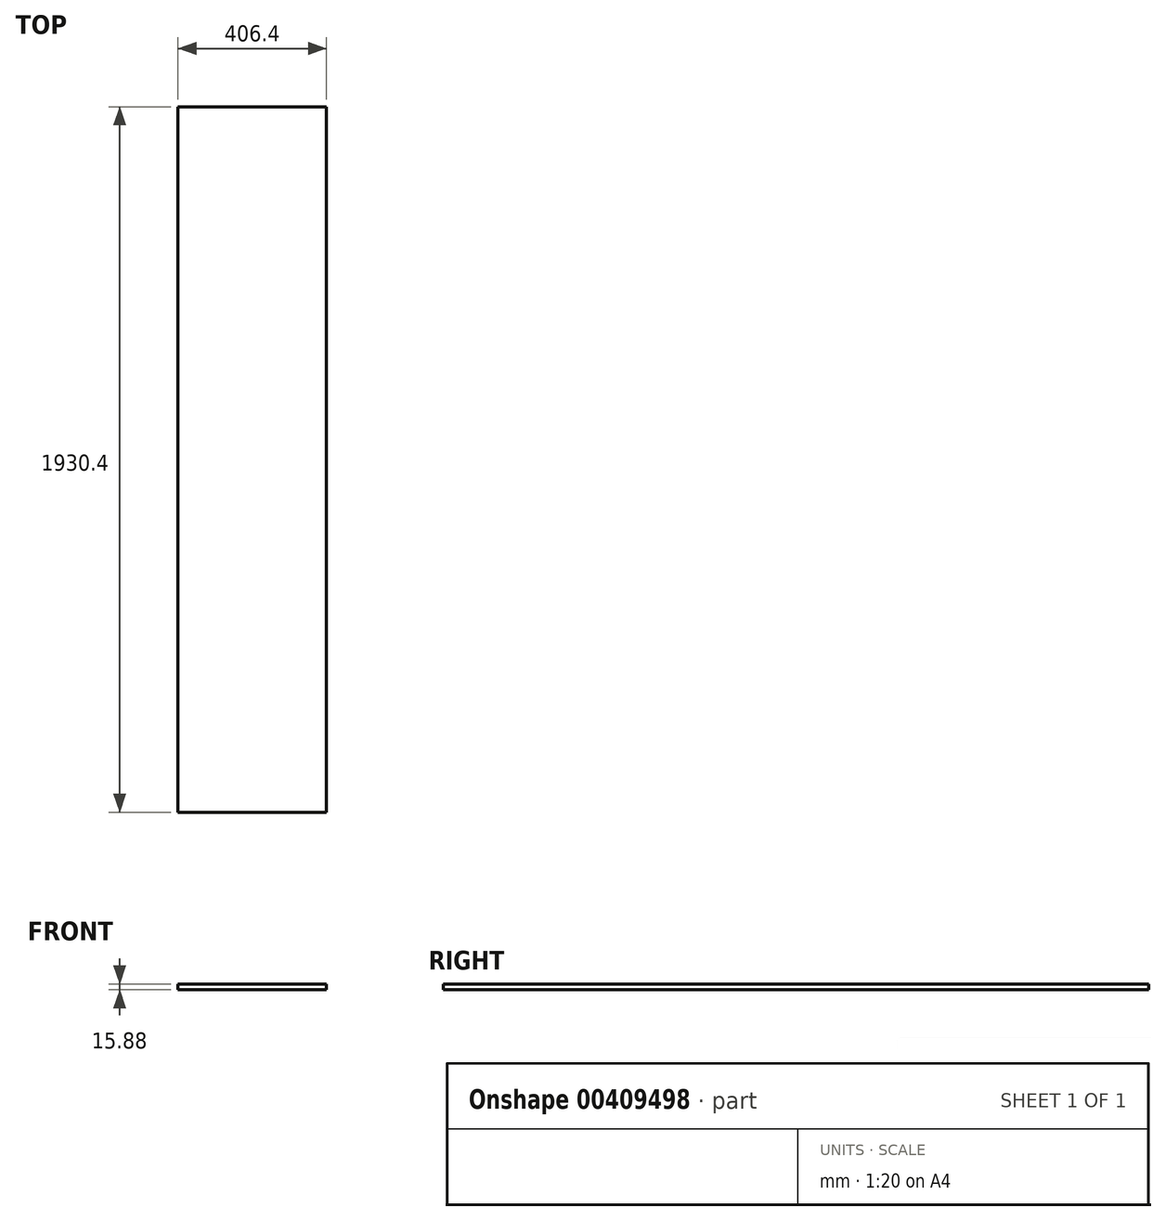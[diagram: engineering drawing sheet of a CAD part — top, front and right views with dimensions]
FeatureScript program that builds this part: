
annotation { "Feature Type Name" : "Feature", "Feature Type Description" : "" }
export const myFeature = defineFeature(function(context is Context, id is Id, definition is map)
    precondition{}
    {
        {
            var Q0;
            Q0=qCreatedBy(makeId("Front.planeOp"),FACE);
            var sketch = newSketch(context, id + "F0", { "sketchPlane" : qUnion([Q0])});
            skLineSegment(sketch, "E0.bottom", {"start": v(0, 0) * mm, "end": v(0, 0) * mm});
            skLineSegment(sketch, "E1.bottom", {"start": v(0, 0) * mm, "end": v(406.4, 0) * mm});
            skLineSegment(sketch, "E1.top", {"start": v(0, 15.87) * mm, "end": v(406.4, 15.87) * mm});
            skLineSegment(sketch, "E1.left", {"start": v(0, 0) * mm, "end": v(0, 15.87) * mm});
            skLineSegment(sketch, "E1.right", {"start": v(406.4, 0) * mm, "end": v(406.4, 15.87) * mm});
            skSolve(sketch);
        }
        {
            var Q0;
            Q0=makeQuery(id+"F0.imprint","IMPRINT",FACE,{"disambiguationData":[TD([[makeQuery(id+"F0.imprint","IMPRINT",EDGE,{"derivedFrom":sQuery(id+"F0.wireOp",EDGE,"E1.bottom")}),1.0]])]});
            extrude(context, id + "F1", {"entities" : qUnion([Q0]), "depth" : 1930.4 * mm});
        }
    });
